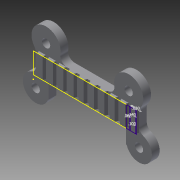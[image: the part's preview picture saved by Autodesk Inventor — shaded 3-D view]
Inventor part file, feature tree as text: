
AUTODESK INVENTOR PART (.ipt)
format: ipt  version: 2013 SP2 (Build 170200200, 200)  size: 280,064 bytes
history: native  units: in
note: dims shown in document units (in); Inventor stores cm internally (conversion verified against a paired STEP export)
features: fillet x6, sketch x6, extrude x5
ambient origin geometry x8: Origin, YZ Plane, XZ Plane, XY Plane, X Axis, Y Axis, Z Axis, Center Point
bodies: Solid1 (feature_tree)
feature tree (17):
  extrude  "Extrusion1"  Depth=0.16in
  fillet  "Fillet1"  Radius=0.4in
  fillet  "Fillet2"  Radius=2.0in
  fillet  "Fillet3"  Radius=0.25in
  fillet  "Fillet4"  Radius=0.125in
  fillet  "Fillet5"  Radius=0.125in
  fillet  "Fillet6"  Radius=0.125in
  extrude  "Extrusion2"  Depth=0.125in
  sketch  "Sketch3"  dims[d40=0.125in d43=2.0in]
  extrude  "Extrusion3"  Depth=2.0in
  extrude  "Extrusion4"  Depth=0.14in
  extrude  "Extrusion6"  Depth=0.02in
  sketch  "Sketch1"  dims[d28=0.4693in d29=0.16in d30=0.4in d31=2.0in d33=0.25in d34=0.0in d35=0.125in d36=0.125in d37=0.125in]
  sketch  "Sketch2"  dims[d38=0.125in d39=0.125in]
  sketch  "Sketch4"  dims[d69=0.049in d70=0.0in d71=0.14in]
  sketch  "Sketch5"  dims[d72=0.06in d73=0.02in]
  sketch  "Sketch9"  dims[d74=0.1in d75=0.02in d76=1.0in d77=0.0in d78=0.14in d80=0.06in d82=0.06in d83=0.06in d84=0.06in d85=0.06in d86=0.06in d87=0.06in d88=0.06in d89=0.06in d90=0.06in d91=1.0in d92=0.0in d100=1.5in d102=0.1in d103=0.0in]
